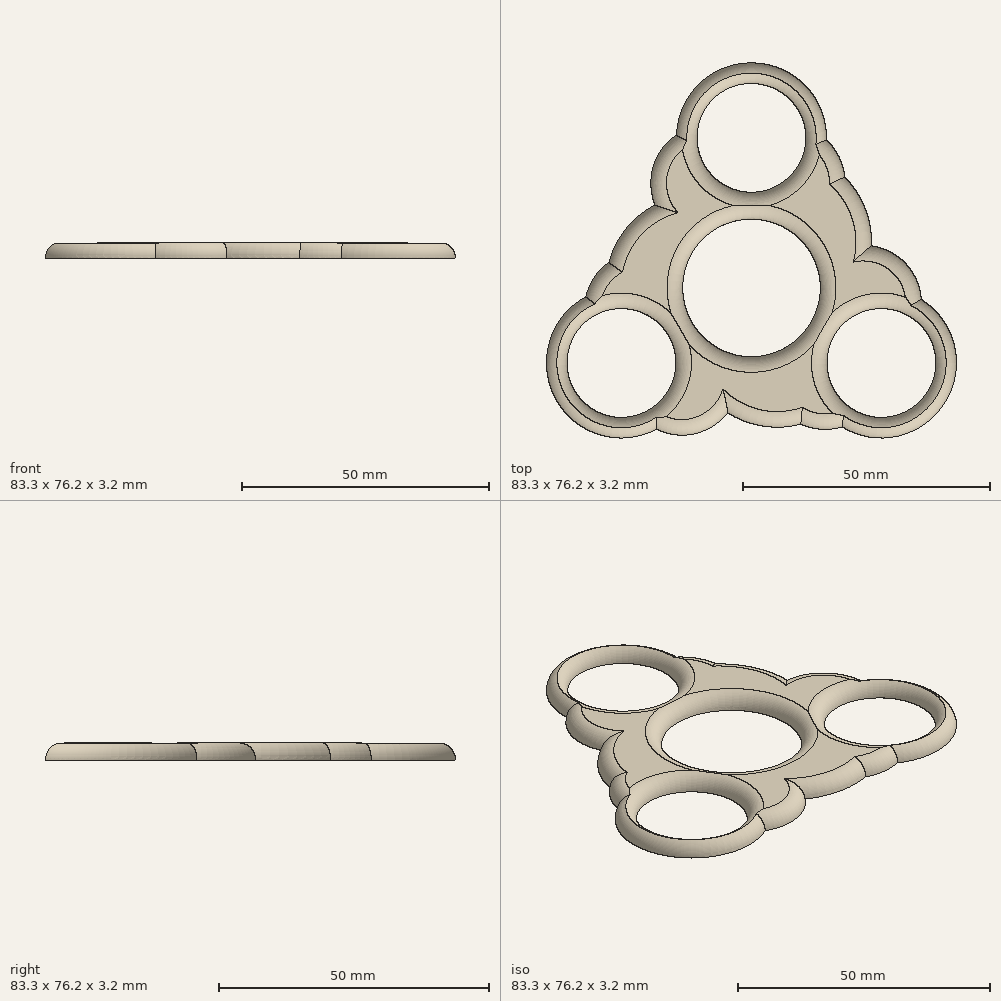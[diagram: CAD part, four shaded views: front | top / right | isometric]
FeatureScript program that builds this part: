
annotation { "Feature Type Name" : "Feature", "Feature Type Description" : "" }
export const myFeature = defineFeature(function(context is Context, id is Id, definition is map)
    precondition{}
    {
        {
            var Q0;
            Q0=qCreatedBy(makeId("Top.planeOp"),FACE);
            var sketch = newSketch(context, id + "F0", { "sketchPlane" : qUnion([Q0])});
            skCircle(sketch, "E0", {"center": v(0, 0) * mm, "radius": 11.05 * mm});
            skCircle(sketch, "E1", {"center": v(0, 0) * mm, "radius": 13.97 * mm});
            skLineSegment(sketch, "E2", {"start": v(0, 0) * mm, "end": v(0, 30.48) * mm});
            skCircle(sketch, "E3", {"center": v(0, 30.48) * mm, "radius": 15.24 * mm});
            skCircle(sketch, "E4", {"center": v(0, 30.48) * mm, "radius": 11.05 * mm});
            skCircle(sketch, "E5.1.0", {"center": v(-26.4, -15.24) * mm, "radius": 15.24 * mm});
            skCircle(sketch, "E5.1.1", {"center": v(-26.4, -15.24) * mm, "radius": 11.05 * mm});
            skCircle(sketch, "E5.2.0", {"center": v(26.4, -15.24) * mm, "radius": 15.24 * mm});
            skCircle(sketch, "E5.2.1", {"center": v(26.4, -15.24) * mm, "radius": 11.05 * mm});
            skArc(sketch, "E6", {"start": v(10.06, 9.7) * mm, "mid": v(18.64, 18.35) * mm, "end": v(15.23, 30.06) * mm});
            skArc(sketch, "E7", {"start": v(21.43, -0.83) * mm, "mid": v(24.29, 11.27) * mm, "end": v(18.95, 22.5) * mm});
            skArc(sketch, "E8", {"start": v(34.5, -2.33) * mm, "mid": v(31.36, 4.9) * mm, "end": v(24.38, 8.55) * mm});
            skArc(sketch, "E9.1.0", {"start": v(-13.42, 3.87) * mm, "mid": v(-25.21, 6.97) * mm, "end": v(-33.65, -1.84) * mm});
            skArc(sketch, "E9.1.1", {"start": v(-10, 18.98) * mm, "mid": v(-21.9, 15.4) * mm, "end": v(-28.97, 5.16) * mm});
            skArc(sketch, "E9.1.2", {"start": v(-15.23, 31.03) * mm, "mid": v(-19.93, 24.7) * mm, "end": v(-19.6, 16.84) * mm});
            skArc(sketch, "E9.2.0", {"start": v(3.36, -13.56) * mm, "mid": v(6.57, -25.32) * mm, "end": v(18.41, -28.22) * mm});
            skArc(sketch, "E9.2.1", {"start": v(-11.44, -18.15) * mm, "mid": v(-2.38, -26.67) * mm, "end": v(10.01, -27.67) * mm});
            skArc(sketch, "E9.2.2", {"start": v(-19.26, -28.7) * mm, "mid": v(-11.43, -29.61) * mm, "end": v(-4.78, -25.39) * mm});
            skSolve(sketch);
        }
        {
            var Q0;
            Q0 = qSketchRegion(id + "F0", true);
            extrude(context, id + "F1", {"entities" : qUnion([Q0]), "depth" : 3.17 * mm, "offsetDistance" : 25.4 * mm});
        }
        {
            var Q0;
            Q0=makeQuery(id+"F1.opExtrude","CAP_FACE",FACE,{"disambiguationData":[OSD([sQuery(id+"F0.wireOp",EDGE,"E1"),sQuery(id+"F0.wireOp",EDGE,"E3"),sQuery(id+"F0.wireOp",EDGE,"E4"),sQuery(id+"F0.wireOp",EDGE,"E5.1.0"),sQuery(id+"F0.wireOp",EDGE,"E5.1.1"),sQuery(id+"F0.wireOp",EDGE,"E5.2.0"),sQuery(id+"F0.wireOp",EDGE,"E5.2.1"),sQuery(id+"F0.wireOp",EDGE,"E6"),sQuery(id+"F0.wireOp",EDGE,"E7"),sQuery(id+"F0.wireOp",EDGE,"E8"),sQuery(id+"F0.wireOp",EDGE,"E9.1.0"),sQuery(id+"F0.wireOp",EDGE,"E9.1.1"),sQuery(id+"F0.wireOp",EDGE,"E9.1.2"),sQuery(id+"F0.wireOp",EDGE,"E9.2.0"),sQuery(id+"F0.wireOp",EDGE,"E9.2.1"),sQuery(id+"F0.wireOp",EDGE,"E9.2.2")])],"isStart":false});
            fillet(context, id + "F2", {"entities" : qUnion([Q0]), "radius" : 3.17 * mm, "tangentPropagation" : true, "allowEdgeOverflow" : false});
        }
    });
